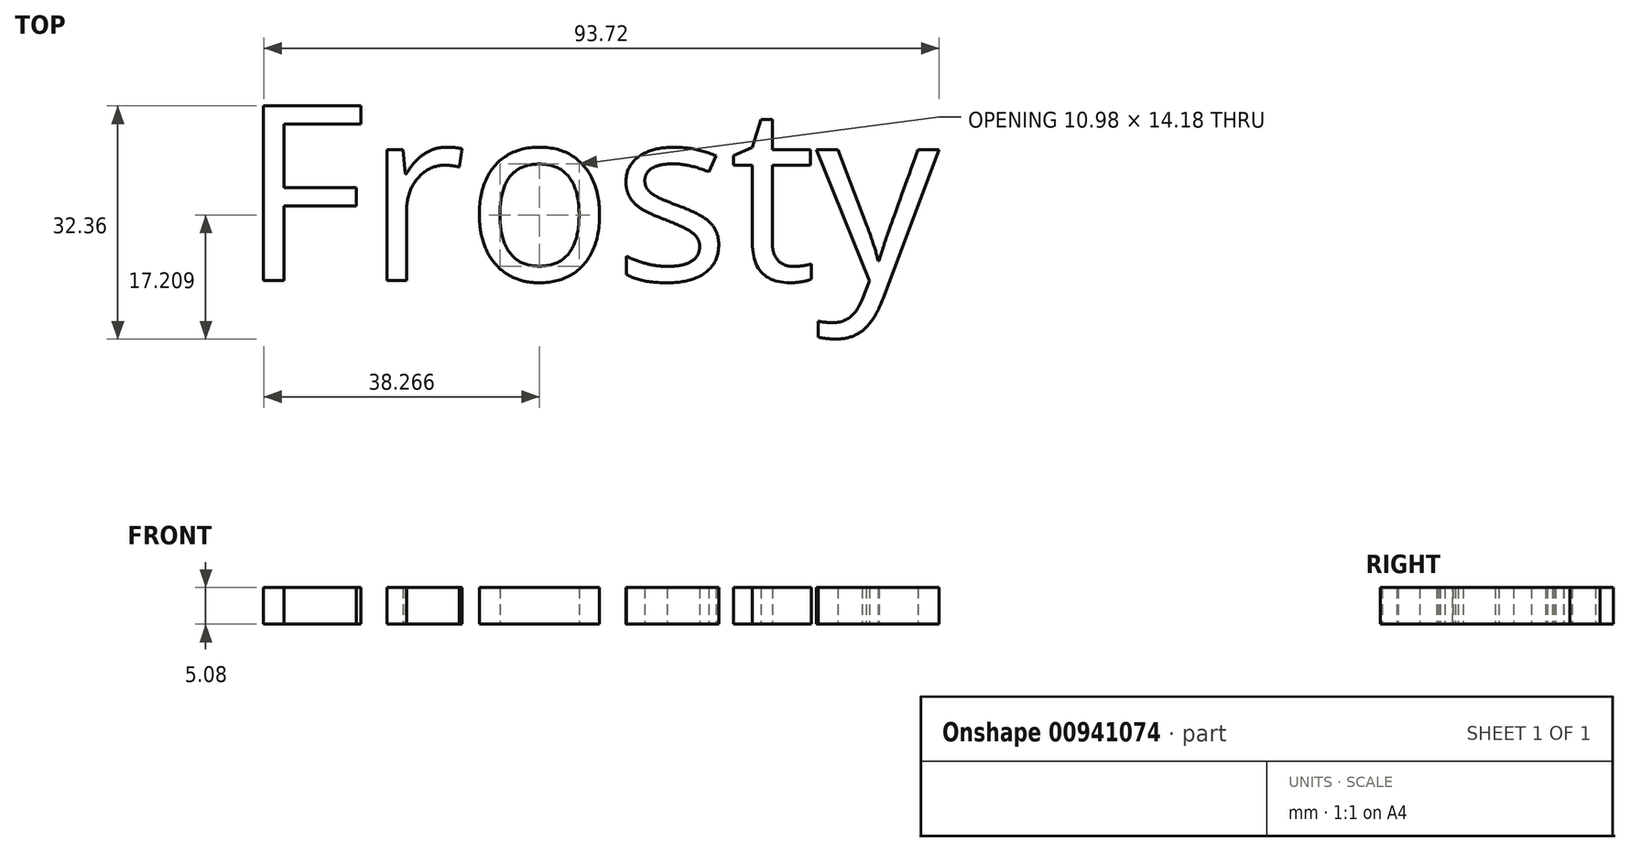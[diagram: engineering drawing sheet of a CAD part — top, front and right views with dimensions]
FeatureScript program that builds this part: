
annotation { "Feature Type Name" : "Feature", "Feature Type Description" : "" }
export const myFeature = defineFeature(function(context is Context, id is Id, definition is map)
    precondition{}
    {
        {
            var Q0;
            Q0=qCreatedBy(makeId("Top.planeOp"),FACE);
            var sketch = newSketch(context, id + "F0", { "sketchPlane" : qUnion([Q0])});
            skText(sketch, "E0", { "text": "Frosty", "fontName": "OpenSans-Regular.ttf"});
            const initialGuessF0  = {"E0": [-0.04962, -0.0195, 1, 0, 0.02442]};
            skSetInitialGuess(sketch, initialGuessF0);
            skSolve(sketch);
        }
        {
            var Q0;
            Q0 = qSketchRegion(id + "F0", true);
            extrude(context, id + "F1", {"entities" : qUnion([Q0]), "depth" : 5.08 * mm, "offsetDistance" : 25.4 * mm});
        }
    });
